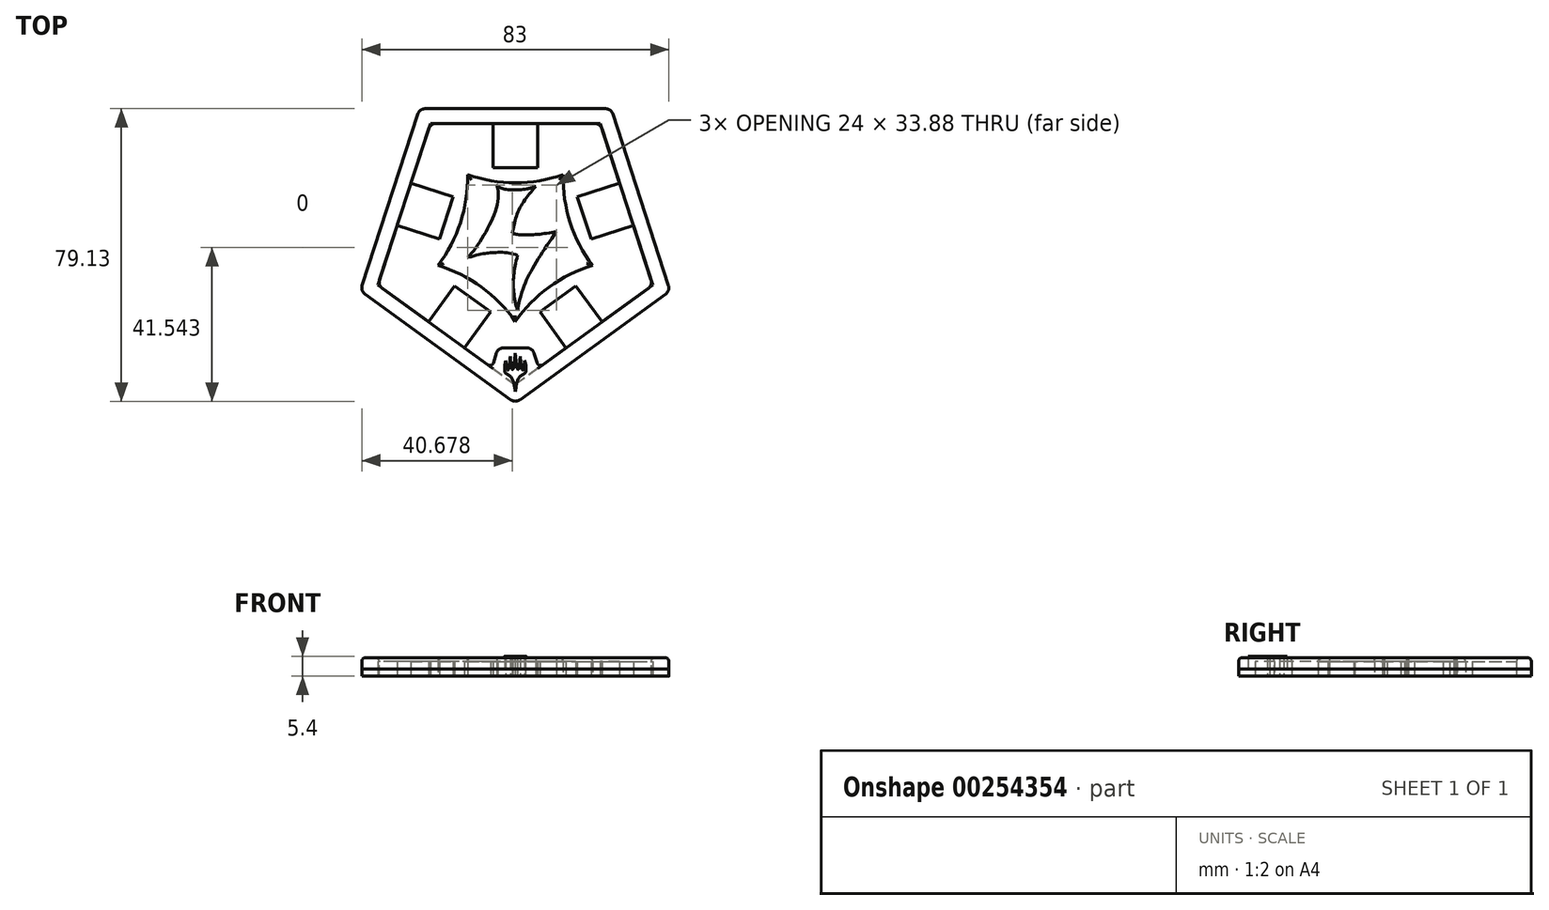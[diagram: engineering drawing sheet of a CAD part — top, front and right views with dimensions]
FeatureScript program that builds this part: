
annotation { "Feature Type Name" : "Feature", "Feature Type Description" : "" }
export const myFeature = defineFeature(function(context is Context, id is Id, definition is map)
    precondition{}
    {
        {
            var Q0;
            Q0=qCreatedBy(makeId("Top.planeOp"),FACE);
            var sketch = newSketch(context, id + "F0", { "sketchPlane" : qUnion([Q0])});
            skCircle(sketch, "E0.cCircle", {"center": v(0, 0) * mm, "radius": 44 * mm, "construction": true});
            skLineSegment(sketch, "E0.0", {"start": v(41.85, -13.6) * mm, "end": v(0, -44) * mm});
            skLineSegment(sketch, "E0.1", {"start": v(0, -44) * mm, "end": v(-41.85, -13.6) * mm});
            skLineSegment(sketch, "E0.2", {"start": v(-41.85, -13.6) * mm, "end": v(-25.86, 35.6) * mm});
            skLineSegment(sketch, "E0.3", {"start": v(-25.86, 35.6) * mm, "end": v(25.86, 35.6) * mm});
            skLineSegment(sketch, "E0.4", {"start": v(25.86, 35.6) * mm, "end": v(41.85, -13.6) * mm});
            skLineSegment(sketch, "E1", {"start": v(-33.85, 11) * mm, "end": v(-24.34, 7.9) * mm, "construction": true});
            skLineSegment(sketch, "E2.bottom", {"start": v(-20.5, 0.35) * mm, "end": v(-31.9, 4.06) * mm});
            skLineSegment(sketch, "E2.top", {"start": v(-16.78, 11.76) * mm, "end": v(-28.2, 15.47) * mm});
            skLineSegment(sketch, "E2.left", {"start": v(-20.5, 0.35) * mm, "end": v(-16.78, 11.76) * mm});
            skLineSegment(sketch, "E2.right", {"start": v(-31.9, 4.06) * mm, "end": v(-28.2, 15.47) * mm});
            skPoint(sketch, "E2.middle", {"position": v(-24.34, 7.9) * mm});
            skLineSegment(sketch, "E3.1.0", {"start": v(-6.66, -19.38) * mm, "end": v(-13.72, -29.09) * mm});
            skLineSegment(sketch, "E3.1.1", {"start": v(-6.66, -19.38) * mm, "end": v(-16.37, -12.33) * mm});
            skLineSegment(sketch, "E3.1.2", {"start": v(-16.37, -12.33) * mm, "end": v(-23.43, -22.04) * mm});
            skLineSegment(sketch, "E3.1.3", {"start": v(-13.72, -29.09) * mm, "end": v(-23.43, -22.04) * mm});
            skPoint(sketch, "E3.1.4", {"position": v(-15.05, -20.7) * mm});
            skLineSegment(sketch, "E3.1.5", {"start": v(-20.92, -28.8) * mm, "end": v(-15.05, -20.7) * mm, "construction": true});
            skLineSegment(sketch, "E3.2.0", {"start": v(16.37, -12.33) * mm, "end": v(23.43, -22.04) * mm});
            skLineSegment(sketch, "E3.2.1", {"start": v(16.37, -12.33) * mm, "end": v(6.66, -19.38) * mm});
            skLineSegment(sketch, "E3.2.2", {"start": v(6.66, -19.38) * mm, "end": v(13.72, -29.09) * mm});
            skLineSegment(sketch, "E3.2.3", {"start": v(23.43, -22.04) * mm, "end": v(13.72, -29.09) * mm});
            skPoint(sketch, "E3.2.4", {"position": v(15.05, -20.7) * mm});
            skLineSegment(sketch, "E3.2.5", {"start": v(20.92, -28.8) * mm, "end": v(15.05, -20.7) * mm, "construction": true});
            skLineSegment(sketch, "E3.3.0", {"start": v(16.78, 11.76) * mm, "end": v(28.2, 15.47) * mm});
            skLineSegment(sketch, "E3.3.1", {"start": v(16.78, 11.76) * mm, "end": v(20.5, 0.35) * mm});
            skLineSegment(sketch, "E3.3.2", {"start": v(20.5, 0.35) * mm, "end": v(31.9, 4.06) * mm});
            skLineSegment(sketch, "E3.3.3", {"start": v(28.2, 15.47) * mm, "end": v(31.9, 4.06) * mm});
            skPoint(sketch, "E3.3.4", {"position": v(24.34, 7.9) * mm});
            skLineSegment(sketch, "E3.3.5", {"start": v(33.85, 11) * mm, "end": v(24.34, 7.9) * mm, "construction": true});
            skLineSegment(sketch, "E3.4.0", {"start": v(-6, 19.6) * mm, "end": v(-6, 31.6) * mm});
            skLineSegment(sketch, "E3.4.1", {"start": v(-6, 19.6) * mm, "end": v(6, 19.6) * mm});
            skLineSegment(sketch, "E3.4.2", {"start": v(6, 19.6) * mm, "end": v(6, 31.6) * mm});
            skLineSegment(sketch, "E3.4.3", {"start": v(-6, 31.6) * mm, "end": v(6, 31.6) * mm});
            skPoint(sketch, "E3.4.4", {"position": v(0, 25.6) * mm});
            skLineSegment(sketch, "E3.4.5", {"start": v(0, 35.6) * mm, "end": v(0, 25.6) * mm, "construction": true});
            skCircle(sketch, "E4.cCircle", {"center": v(0, 0) * mm, "radius": 22 * mm, "construction": true});
            skLineSegment(sketch, "E4.0", {"start": v(20.92, -6.8) * mm, "end": v(0, -22) * mm, "construction": true});
            skLineSegment(sketch, "E4.1", {"start": v(0, -22) * mm, "end": v(-20.92, -6.8) * mm, "construction": true});
            skLineSegment(sketch, "E4.2", {"start": v(-20.92, -6.8) * mm, "end": v(-12.93, 17.8) * mm, "construction": true});
            skLineSegment(sketch, "E4.3", {"start": v(-12.93, 17.8) * mm, "end": v(12.93, 17.8) * mm, "construction": true});
            skLineSegment(sketch, "E4.4", {"start": v(12.93, 17.8) * mm, "end": v(20.92, -6.8) * mm, "construction": true});
            skLineSegment(sketch, "E5", {"start": v(-24.34, 7.9) * mm, "end": v(-14.83, 4.82) * mm, "construction": true});
            skArc(sketch, "E6", {"start": v(-20.92, -6.8) * mm, "mid": v(-14.83, 4.82) * mm, "end": v(-12.93, 17.8) * mm});
            skArc(sketch, "E7.1.0", {"start": v(0, -22) * mm, "mid": v(-9.17, -12.62) * mm, "end": v(-20.92, -6.8) * mm});
            skArc(sketch, "E7.2.0", {"start": v(20.92, -6.8) * mm, "mid": v(9.17, -12.62) * mm, "end": v(0, -22) * mm});
            skArc(sketch, "E7.3.0", {"start": v(12.93, 17.8) * mm, "mid": v(14.83, 4.82) * mm, "end": v(20.92, -6.8) * mm});
            skArc(sketch, "E7.4.0", {"start": v(-12.93, 17.8) * mm, "mid": v(0, 15.6) * mm, "end": v(12.93, 17.8) * mm});
            skLineSegment(sketch, "E8", {"start": v(-41.85, -13.6) * mm, "end": v(0, 0) * mm, "construction": true});
            skLineSegment(sketch, "E9", {"start": v(-31.9, 4.06) * mm, "end": v(-37.14, -12.07) * mm});
            skLineSegment(sketch, "E10", {"start": v(0, 0) * mm, "end": v(-25.86, 35.6) * mm, "construction": true});
            skLineSegment(sketch, "E11", {"start": v(-28.2, 15.47) * mm, "end": v(-22.96, 31.6) * mm});
            skLineSegment(sketch, "E12.1.0", {"start": v(-13.72, -29.09) * mm, "end": v(0, -39.06) * mm});
            skLineSegment(sketch, "E12.1.1", {"start": v(-23.43, -22.04) * mm, "end": v(-37.14, -12.07) * mm});
            skLineSegment(sketch, "E12.2.0", {"start": v(23.43, -22.04) * mm, "end": v(37.14, -12.07) * mm});
            skLineSegment(sketch, "E12.2.1", {"start": v(13.72, -29.09) * mm, "end": v(0, -39.06) * mm});
            skLineSegment(sketch, "E12.3.0", {"start": v(28.2, 15.47) * mm, "end": v(22.96, 31.6) * mm});
            skLineSegment(sketch, "E12.3.1", {"start": v(31.9, 4.06) * mm, "end": v(37.14, -12.07) * mm});
            skLineSegment(sketch, "E12.4.0", {"start": v(-6, 31.6) * mm, "end": v(-22.96, 31.6) * mm});
            skLineSegment(sketch, "E12.4.1", {"start": v(6, 31.6) * mm, "end": v(22.96, 31.6) * mm});
            skSolve(sketch);
        }
        {
            var Q0;
            Q0=qCreatedBy(makeId("Top.planeOp"),FACE);
            var sketch = newSketch(context, id + "F1", { "sketchPlane" : qUnion([Q0])});
            skFitSpline(sketch, "E13", {"points": [v(-5, 14.95) * mm, v(-1.02, 13.68) * mm, v(5.52, 14.64) * mm], "startDerivative": vector(6.48, -7.02) * mm, "endDerivative": vector(9.45, 4.73) * mm});
            skFitSpline(sketch, "E14", {"points": [v(5.52, 14.64) * mm, v(0.97, 8.26) * mm, v(-0.78, 1.88) * mm], "startDerivative": vector(-10.05, -11.93) * mm, "endDerivative": vector(-2.28, -13.44) * mm});
            skFitSpline(sketch, "E15", {"points": [v(-0.78, 1.88) * mm, v(2.89, 1.48) * mm, v(11.18, 2.36) * mm], "startDerivative": vector(7.53, -2.38) * mm, "endDerivative": vector(15.6, 3.22) * mm});
            skFitSpline(sketch, "E16", {"points": [v(11.18, 2.36) * mm, v(4.32, -8.24) * mm, v(0.57, -18.93) * mm], "startDerivative": vector(-15.33, -20.77) * mm, "endDerivative": vector(-6.9, -33.93) * mm});
            skFitSpline(sketch, "E17", {"points": [v(0.57, -18.93) * mm, v(-0.54, -11.83) * mm, v(0.57, -4.1) * mm], "startDerivative": vector(-3.94, 12.93) * mm, "endDerivative": vector(3.74, 16.63) * mm});
            skFitSpline(sketch, "E18", {"points": [v(0.57, -4.1) * mm, v(-5.89, -3.3) * mm, v(-12.82, -4.66) * mm], "startDerivative": vector(-11.71, 5.86) * mm, "endDerivative": vector(-20.63, -6.1) * mm});
            skFitSpline(sketch, "E19", {"points": [v(-12.82, -4.66) * mm, v(-6.6, 4.9) * mm, v(-5, 14.95) * mm], "startDerivative": vector(11.21, 11.67) * mm, "endDerivative": vector(-5.9, 20.2) * mm});
            skSolve(sketch);
        }
        {
            var Q0;
            Q0=qCreatedBy(makeId("Top.planeOp"),FACE);
            var sketch = newSketch(context, id + "F2", { "sketchPlane" : qUnion([Q0])});
            skPoint(sketch, "E20.0", {"position": v(0, 0) * mm});
            skLineSegment(sketch, "E21.0.0", {"start": v(41.85, -13.6) * mm, "end": v(25.86, 35.6) * mm});
            skLineSegment(sketch, "E21.0.1", {"start": v(25.86, 35.6) * mm, "end": v(-25.86, 35.6) * mm});
            skLineSegment(sketch, "E21.0.2", {"start": v(-25.86, 35.6) * mm, "end": v(-41.85, -13.6) * mm});
            skLineSegment(sketch, "E21.0.3", {"start": v(-41.85, -13.6) * mm, "end": v(0, -44) * mm});
            skLineSegment(sketch, "E21.0.4", {"start": v(0, -44) * mm, "end": v(41.85, -13.6) * mm});
            skLineSegment(sketch, "E22.1", {"start": v(-13.72, -29.09) * mm, "end": v(-23.43, -22.04) * mm});
            skLineSegment(sketch, "E22.2", {"start": v(-23.43, -22.04) * mm, "end": v(-37.14, -12.07) * mm});
            skLineSegment(sketch, "E22.3", {"start": v(-31.9, 4.06) * mm, "end": v(-37.14, -12.07) * mm});
            skLineSegment(sketch, "E22.4", {"start": v(-31.9, 4.06) * mm, "end": v(-28.2, 15.47) * mm});
            skLineSegment(sketch, "E22.5", {"start": v(-28.2, 15.47) * mm, "end": v(-22.96, 31.6) * mm});
            skLineSegment(sketch, "E22.7", {"start": v(23.43, -22.04) * mm, "end": v(13.72, -29.09) * mm});
            skLineSegment(sketch, "E22.8", {"start": v(23.43, -22.04) * mm, "end": v(37.14, -12.07) * mm});
            skLineSegment(sketch, "E22.9", {"start": v(31.9, 4.06) * mm, "end": v(37.14, -12.07) * mm});
            skLineSegment(sketch, "E22.10", {"start": v(28.2, 15.47) * mm, "end": v(31.9, 4.06) * mm});
            skLineSegment(sketch, "E22.11", {"start": v(28.2, 15.47) * mm, "end": v(22.96, 31.6) * mm});
            skLineSegment(sketch, "E22.12", {"start": v(6, 31.6) * mm, "end": v(22.96, 31.6) * mm});
            skLineSegment(sketch, "E22.13", {"start": v(-6, 31.6) * mm, "end": v(6, 31.6) * mm});
            skLineSegment(sketch, "E22.14", {"start": v(-6, 31.6) * mm, "end": v(-22.96, 31.6) * mm});
            skLineSegment(sketch, "E23", {"start": v(-13.72, -29.09) * mm, "end": v(-6.31, -34.47) * mm});
            skLineSegment(sketch, "E24", {"start": v(-6.31, -34.47) * mm, "end": v(-4.65, -29.09) * mm});
            skLineSegment(sketch, "E25", {"start": v(13.72, -29.09) * mm, "end": v(6.31, -34.47) * mm});
            skLineSegment(sketch, "E26", {"start": v(6.31, -34.47) * mm, "end": v(4.57, -29.09) * mm});
            skLineSegment(sketch, "E27", {"start": v(4.57, -29.09) * mm, "end": v(-4.65, -29.09) * mm});
            skSolve(sketch);
        }
        {
            var Q0;
            Q0=qCreatedBy(makeId("Top.planeOp"),FACE);
            var sketch = newSketch(context, id + "F3", { "sketchPlane" : qUnion([Q0])});
            skFitSpline(sketch, "E28", {"points": [v(0, -30.45) * mm, v(-0.66, -34.88) * mm, v(-1.34, -31.36) * mm], "startDerivative": vector(-1.52, -19.16) * mm, "endDerivative": vector(-1.65, 22.93) * mm});
            skFitSpline(sketch, "E29", {"points": [v(-1.34, -31.36) * mm, v(-2.03, -35.13) * mm, v(-2.53, -32.49) * mm], "startDerivative": vector(-1.22, -16.23) * mm, "endDerivative": vector(-0.98, 14.27) * mm});
            skFitSpline(sketch, "E30", {"points": [v(-2.53, -32.49) * mm, v(-2.9, -34.67) * mm, v(-2.8, -35.7) * mm], "startDerivative": vector(-1.89, -5.29) * mm, "endDerivative": vector(0.95, -1.62) * mm});
            skFitSpline(sketch, "E31", {"points": [v(-2.8, -35.7) * mm, v(-1.08, -37.06) * mm, v(0, -40.97) * mm], "startDerivative": vector(2.36, -2.75) * mm, "endDerivative": vector(1.27, -7.94) * mm});
            skFitSpline(sketch, "E32.MirrorCS", {"points": [v(0, -30.45) * mm, v(0.66, -34.88) * mm, v(1.34, -31.36) * mm], "startDerivative": vector(1.52, -19.16) * mm, "endDerivative": vector(1.65, 22.93) * mm});
            skFitSpline(sketch, "E33.MirrorCS", {"points": [v(1.34, -31.36) * mm, v(2.03, -35.13) * mm, v(2.53, -32.49) * mm], "startDerivative": vector(1.22, -16.23) * mm, "endDerivative": vector(0.98, 14.27) * mm});
            skFitSpline(sketch, "E34.MirrorCS", {"points": [v(2.53, -32.49) * mm, v(2.9, -34.67) * mm, v(2.8, -35.7) * mm], "startDerivative": vector(1.89, -5.29) * mm, "endDerivative": vector(-0.95, -1.62) * mm});
            skFitSpline(sketch, "E35.MirrorCS", {"points": [v(2.8, -35.7) * mm, v(1.08, -37.06) * mm, v(0, -40.97) * mm], "startDerivative": vector(-2.36, -2.75) * mm, "endDerivative": vector(-1.27, -7.94) * mm});
            skSolve(sketch);
        }
        {
            var Q0;
            Q0=makeQuery(id+"F2.imprint","IMPRINT",FACE,{"disambiguationData":[TD([[makeQuery(id+"F2.imprint","IMPRINT",EDGE,{"derivedFrom":sQuery(id+"F2.wireOp",EDGE,"E21.0.0")}),1.0]])]});
            var Q1;
            Q1=makeQuery(id+"F0.imprint","IMPRINT",FACE,{"disambiguationData":[TD([[makeQuery(id+"F0.imprint","IMPRINT",EDGE,{"derivedFrom":sQuery(id+"F0.wireOp",EDGE,"E6")}),-1.0]])]});
            var Q2;
            Q2=makeQuery(id+"F0.imprint","IMPRINT",FACE,{"disambiguationData":[TD([[makeQuery(id+"F0.imprint","IMPRINT",EDGE,{"derivedFrom":sQuery(id+"F0.wireOp",EDGE,"E2.bottom")}),1.0]])]});
            var Q3;
            Q3=makeQuery(id+"F2.imprint","IMPRINT",FACE,{"disambiguationData":[TD([[makeQuery(id+"F2.imprint","IMPRINT",EDGE,{"derivedFrom":sQuery(id+"F2.wireOp",EDGE,"E22.1")}),-1.0]])]});
            extrude(context, id + "F4", {"entities" : qUnion([Q0, Q1, Q2, Q3]), "depth" : 2 * mm});
        }
        {
            var Q0;
            Q0 = qSketchRegion(id + "F2", true);
            extrude(context, id + "F5", {"entities" : qUnion([Q0]), "depth" : 5 * mm});
        }
        {
            var Q0;
            Q0=makeQuery(id+"F4.opExtrude","CAP_FACE",FACE,{"disambiguationData":[OSD([sQuery(id+"F0.wireOp",EDGE,"E2.bottom"),sQuery(id+"F0.wireOp",EDGE,"E2.top"),sQuery(id+"F0.wireOp",EDGE,"E2.left"),sQuery(id+"F0.wireOp",EDGE,"E3.1.0"),sQuery(id+"F0.wireOp",EDGE,"E3.1.1"),sQuery(id+"F0.wireOp",EDGE,"E3.1.2"),sQuery(id+"F0.wireOp",EDGE,"E3.2.0"),sQuery(id+"F0.wireOp",EDGE,"E3.2.1"),sQuery(id+"F0.wireOp",EDGE,"E3.2.2"),sQuery(id+"F0.wireOp",EDGE,"E3.3.0"),sQuery(id+"F0.wireOp",EDGE,"E3.3.1"),sQuery(id+"F0.wireOp",EDGE,"E3.3.2"),sQuery(id+"F0.wireOp",EDGE,"E3.4.0"),sQuery(id+"F0.wireOp",EDGE,"E3.4.1"),sQuery(id+"F0.wireOp",EDGE,"E3.4.2"),sQuery(id+"F0.wireOp",EDGE,"E9"),sQuery(id+"F0.wireOp",EDGE,"E11"),sQuery(id+"F0.wireOp",EDGE,"E12.1.0"),sQuery(id+"F0.wireOp",EDGE,"E12.1.1"),sQuery(id+"F0.wireOp",EDGE,"E12.2.0"),sQuery(id+"F0.wireOp",EDGE,"E12.2.1"),sQuery(id+"F0.wireOp",EDGE,"E12.3.0"),sQuery(id+"F0.wireOp",EDGE,"E12.3.1"),sQuery(id+"F0.wireOp",EDGE,"E12.4.0"),sQuery(id+"F0.wireOp",EDGE,"E12.4.1")])],"isStart":false});
            extrude(context, id + "F6", {"entities" : qUnion([Q0]), "depth" : 2 * mm});
        }
        {
            var Q0;
            Q0=qCreatedBy(makeId("Top.planeOp"),FACE);
            var sketch = newSketch(context, id + "F7", { "sketchPlane" : qUnion([Q0])});
            skArc(sketch, "E36.0", {"start": v(-20.92, -6.8) * mm, "mid": v(-14.83, 4.82) * mm, "end": v(-12.93, 17.8) * mm});
            skArc(sketch, "E36.1", {"start": v(0, -22) * mm, "mid": v(-9.17, -12.62) * mm, "end": v(-20.92, -6.8) * mm});
            skArc(sketch, "E36.2", {"start": v(20.92, -6.8) * mm, "mid": v(9.17, -12.62) * mm, "end": v(0, -22) * mm});
            skArc(sketch, "E36.3", {"start": v(12.93, 17.8) * mm, "mid": v(14.83, 4.82) * mm, "end": v(20.92, -6.8) * mm});
            skArc(sketch, "E36.4", {"start": v(-12.93, 17.8) * mm, "mid": v(0, 15.6) * mm, "end": v(12.93, 17.8) * mm});
            skSolve(sketch);
        }
        {
            var Q0;
            Q0 = qSketchRegion(id + "F7", true);
            extrude(context, id + "F8", {"entities" : qUnion([Q0]), "depth" : 5 * mm});
        }
        {
            var Q0;
            Q0 = qSketchRegion(id + "F1", true);
            extrude(context, id + "F9", {"entities" : qUnion([Q0]), "operationType" : NewBodyOperationType.REMOVE, "endBound" : BoundingType.THROUGH_ALL, "depth" : 25 * mm});
        }
        {
            var Q0;
            Q0 = qSketchRegion(id + "F3", true);
            var Q1;
            Q1=makeQuery(id+"F5.opExtrude","CAP_FACE",FACE,{"disambiguationData":[OSD([sQuery(id+"F2.wireOp",EDGE,"E21.0.0"),sQuery(id+"F2.wireOp",EDGE,"E21.0.1"),sQuery(id+"F2.wireOp",EDGE,"E21.0.2"),sQuery(id+"F2.wireOp",EDGE,"E21.0.3"),sQuery(id+"F2.wireOp",EDGE,"E21.0.4"),sQuery(id+"F2.wireOp",EDGE,"E22.1"),sQuery(id+"F2.wireOp",EDGE,"E22.2"),sQuery(id+"F2.wireOp",EDGE,"E22.3"),sQuery(id+"F2.wireOp",EDGE,"E22.4"),sQuery(id+"F2.wireOp",EDGE,"E22.5"),sQuery(id+"F2.wireOp",EDGE,"E22.7"),sQuery(id+"F2.wireOp",EDGE,"E22.8"),sQuery(id+"F2.wireOp",EDGE,"E22.9"),sQuery(id+"F2.wireOp",EDGE,"E22.10"),sQuery(id+"F2.wireOp",EDGE,"E22.11"),sQuery(id+"F2.wireOp",EDGE,"E22.12"),sQuery(id+"F2.wireOp",EDGE,"E22.13"),sQuery(id+"F2.wireOp",EDGE,"E22.14"),sQuery(id+"F2.wireOp",EDGE,"E23"),sQuery(id+"F2.wireOp",EDGE,"E24"),sQuery(id+"F2.wireOp",EDGE,"E25"),sQuery(id+"F2.wireOp",EDGE,"E26"),sQuery(id+"F2.wireOp",EDGE,"E27")])],"isStart":false});
            extrude(context, id + "F10", {"entities" : qUnion([Q0]), "endBoundEntityFace" : qUnion([Q1]), "depth" : 5.4 * mm});
        }
        {
            var Q0;
            Q0=makeQuery(id+"F8.opExtrude","CAP_EDGE",EDGE,{"disambiguationData":[OSD([sQuery(id+"F7.wireOp",EDGE,"E36.1")])],"isStart":false});
            var Q1;
            Q1=makeQuery(id+"F8.opExtrude","CAP_EDGE",EDGE,{"disambiguationData":[OSD([sQuery(id+"F7.wireOp",EDGE,"E36.2")])],"isStart":false});
            var Q2;
            Q2=makeQuery(id+"F8.opExtrude","CAP_EDGE",EDGE,{"disambiguationData":[OSD([sQuery(id+"F7.wireOp",EDGE,"E36.3")])],"isStart":false});
            var Q3;
            Q3=makeQuery(id+"F8.opExtrude","CAP_EDGE",EDGE,{"disambiguationData":[OSD([sQuery(id+"F7.wireOp",EDGE,"E36.4")])],"isStart":false});
            var Q4;
            Q4=makeQuery(id+"F8.opExtrude","CAP_EDGE",EDGE,{"disambiguationData":[OSD([sQuery(id+"F7.wireOp",EDGE,"E36.0")])],"isStart":false});
            fillet(context, id + "F11", {"entities" : qUnion([Q0, Q1, Q2, Q3, Q4]), "radius" : 1 * mm, "tangentPropagation" : true, "allowEdgeOverflow" : false});
        }
        {
            var Q0;
            Q0=makeQuery(id+"F5.opExtrude","SWEPT_EDGE",EDGE,{"disambiguationData":[OSD([sQuery(id+"F2.wireOp",EDGE,"E21.0.2"),sQuery(id+"F2.wireOp",EDGE,"E21.0.3")])]});
            var Q1;
            Q1=makeQuery(id+"F4.opExtrude","SWEPT_EDGE",EDGE,{"disambiguationData":[OSD([sQuery(id+"F2.wireOp",EDGE,"E21.0.2"),sQuery(id+"F2.wireOp",EDGE,"E21.0.3")])]});
            var Q2;
            Q2=makeQuery(id+"F4.opExtrude","SWEPT_EDGE",EDGE,{"disambiguationData":[OSD([sQuery(id+"F2.wireOp",EDGE,"E21.0.3"),sQuery(id+"F2.wireOp",EDGE,"E21.0.4")])]});
            var Q3;
            Q3=makeQuery(id+"F5.opExtrude","SWEPT_EDGE",EDGE,{"disambiguationData":[OSD([sQuery(id+"F2.wireOp",EDGE,"E21.0.3"),sQuery(id+"F2.wireOp",EDGE,"E21.0.4")])]});
            var Q4;
            Q4=makeQuery(id+"F5.opExtrude","SWEPT_EDGE",EDGE,{"disambiguationData":[OSD([sQuery(id+"F2.wireOp",EDGE,"E21.0.0"),sQuery(id+"F2.wireOp",EDGE,"E21.0.4")])]});
            var Q5;
            Q5=makeQuery(id+"F4.opExtrude","SWEPT_EDGE",EDGE,{"disambiguationData":[OSD([sQuery(id+"F2.wireOp",EDGE,"E21.0.0"),sQuery(id+"F2.wireOp",EDGE,"E21.0.4")])]});
            var Q6;
            Q6=makeQuery(id+"F5.opExtrude","SWEPT_EDGE",EDGE,{"disambiguationData":[OSD([sQuery(id+"F2.wireOp",EDGE,"E21.0.1"),sQuery(id+"F2.wireOp",EDGE,"E21.0.2")])]});
            var Q7;
            Q7=makeQuery(id+"F4.opExtrude","SWEPT_EDGE",EDGE,{"disambiguationData":[OSD([sQuery(id+"F2.wireOp",EDGE,"E21.0.1"),sQuery(id+"F2.wireOp",EDGE,"E21.0.2")])]});
            var Q8;
            Q8=makeQuery(id+"F5.opExtrude","SWEPT_EDGE",EDGE,{"disambiguationData":[OSD([sQuery(id+"F2.wireOp",EDGE,"E21.0.0"),sQuery(id+"F2.wireOp",EDGE,"E21.0.1")])]});
            var Q9;
            Q9=makeQuery(id+"F4.opExtrude","SWEPT_EDGE",EDGE,{"disambiguationData":[OSD([sQuery(id+"F2.wireOp",EDGE,"E21.0.0"),sQuery(id+"F2.wireOp",EDGE,"E21.0.1")])]});
            var Q10;
            Q10=makeQuery(id+"F5.opExtrude","SWEPT_EDGE",EDGE,{"disambiguationData":[OSD([sQuery(id+"F2.wireOp",EDGE,"E22.11"),sQuery(id+"F2.wireOp",EDGE,"E22.12")])]});
            var Q11;
            Q11=makeQuery(id+"F5.opExtrude","SWEPT_EDGE",EDGE,{"disambiguationData":[OSD([sQuery(id+"F2.wireOp",EDGE,"E22.5"),sQuery(id+"F2.wireOp",EDGE,"E22.14")])]});
            var Q12;
            Q12=makeQuery(id+"F5.opExtrude","SWEPT_EDGE",EDGE,{"disambiguationData":[OSD([sQuery(id+"F2.wireOp",EDGE,"E22.2"),sQuery(id+"F2.wireOp",EDGE,"E22.3")])]});
            var Q13;
            Q13=makeQuery(id+"F5.opExtrude","SWEPT_EDGE",EDGE,{"disambiguationData":[OSD([sQuery(id+"F2.wireOp",EDGE,"E22.8"),sQuery(id+"F2.wireOp",EDGE,"E22.9")])]});
            fillet(context, id + "F12", {"entities" : qUnion([Q0, Q1, Q2, Q3, Q4, Q5, Q6, Q7, Q8, Q9, Q10, Q11, Q12, Q13]), "radius" : 2 * mm, "tangentPropagation" : true, "allowEdgeOverflow" : false});
        }
        {
            var Q0;
            Q0=makeQuery(id+"F5.opExtrude","SWEPT_EDGE",EDGE,{"disambiguationData":[OSD([sQuery(id+"F2.wireOp",EDGE,"E24"),sQuery(id+"F2.wireOp",EDGE,"E27")])]});
            var Q1;
            Q1=makeQuery(id+"F5.opExtrude","SWEPT_EDGE",EDGE,{"disambiguationData":[OSD([sQuery(id+"F2.wireOp",EDGE,"E26"),sQuery(id+"F2.wireOp",EDGE,"E27")])]});
            fillet(context, id + "F13", {"entities" : qUnion([Q0, Q1]), "radius" : 2 * mm, "tangentPropagation" : true, "allowEdgeOverflow" : false});
        }
        {
            var Q0;
            Q0=makeQuery(id+"F5.opExtrude","SWEPT_EDGE",EDGE,{"disambiguationData":[OSD([sQuery(id+"F2.wireOp",EDGE,"E23"),sQuery(id+"F2.wireOp",EDGE,"E24")])]});
            var Q1;
            Q1=makeQuery(id+"F5.opExtrude","SWEPT_EDGE",EDGE,{"disambiguationData":[OSD([sQuery(id+"F2.wireOp",EDGE,"E25"),sQuery(id+"F2.wireOp",EDGE,"E26")])]});
            fillet(context, id + "F14", {"entities" : qUnion([Q0, Q1]), "radius" : 1 * mm, "tangentPropagation" : true, "allowEdgeOverflow" : false});
        }
        {
            var Q0;
            {var subQ0=sQuery(id+"F2.wireOp",EDGE,"E21.0.2");var subQ1=sQuery(id+"F2.wireOp",EDGE,"E21.0.1");Q0=makeQuery(id+"F12.opFillet","BLEND_EDGE",EDGE,{"blendedFrom":[makeQuery(id+"F5.opExtrude","SWEPT_EDGE",EDGE,{"disambiguationData":[OSD([subQ1,subQ0])]}),makeQuery(id+"F5.opExtrude","CAP_FACE",FACE,{"disambiguationData":[OSD([sQuery(id+"F2.wireOp",EDGE,"E21.0.0"),subQ1,subQ0,sQuery(id+"F2.wireOp",EDGE,"E21.0.3"),sQuery(id+"F2.wireOp",EDGE,"E21.0.4"),sQuery(id+"F2.wireOp",EDGE,"E22.1"),sQuery(id+"F2.wireOp",EDGE,"E22.2"),sQuery(id+"F2.wireOp",EDGE,"E22.3"),sQuery(id+"F2.wireOp",EDGE,"E22.4"),sQuery(id+"F2.wireOp",EDGE,"E22.5"),sQuery(id+"F2.wireOp",EDGE,"E22.7"),sQuery(id+"F2.wireOp",EDGE,"E22.8"),sQuery(id+"F2.wireOp",EDGE,"E22.9"),sQuery(id+"F2.wireOp",EDGE,"E22.10"),sQuery(id+"F2.wireOp",EDGE,"E22.11"),sQuery(id+"F2.wireOp",EDGE,"E22.12"),sQuery(id+"F2.wireOp",EDGE,"E22.13"),sQuery(id+"F2.wireOp",EDGE,"E22.14"),sQuery(id+"F2.wireOp",EDGE,"E23"),sQuery(id+"F2.wireOp",EDGE,"E24"),sQuery(id+"F2.wireOp",EDGE,"E25"),sQuery(id+"F2.wireOp",EDGE,"E26"),sQuery(id+"F2.wireOp",EDGE,"E27")])],"isStart":false})],"blendedInto":[makeQuery(id+"F5.opExtrude","CAP_FACE",FACE,{"disambiguationData":[OSD([sQuery(id+"F2.wireOp",EDGE,"E21.0.0"),subQ1,subQ0,sQuery(id+"F2.wireOp",EDGE,"E21.0.3"),sQuery(id+"F2.wireOp",EDGE,"E21.0.4"),sQuery(id+"F2.wireOp",EDGE,"E22.1"),sQuery(id+"F2.wireOp",EDGE,"E22.2"),sQuery(id+"F2.wireOp",EDGE,"E22.3"),sQuery(id+"F2.wireOp",EDGE,"E22.4"),sQuery(id+"F2.wireOp",EDGE,"E22.5"),sQuery(id+"F2.wireOp",EDGE,"E22.7"),sQuery(id+"F2.wireOp",EDGE,"E22.8"),sQuery(id+"F2.wireOp",EDGE,"E22.9"),sQuery(id+"F2.wireOp",EDGE,"E22.10"),sQuery(id+"F2.wireOp",EDGE,"E22.11"),sQuery(id+"F2.wireOp",EDGE,"E22.12"),sQuery(id+"F2.wireOp",EDGE,"E22.13"),sQuery(id+"F2.wireOp",EDGE,"E22.14"),sQuery(id+"F2.wireOp",EDGE,"E23"),sQuery(id+"F2.wireOp",EDGE,"E24"),sQuery(id+"F2.wireOp",EDGE,"E25"),sQuery(id+"F2.wireOp",EDGE,"E26"),sQuery(id+"F2.wireOp",EDGE,"E27")])],"isStart":false})]});}
            fillet(context, id + "F15", {"entities" : qUnion([Q0]), "radius" : 1 * mm, "tangentPropagation" : true, "allowEdgeOverflow" : false});
        }
        {
            var Q0;
            {var subQ0=sQuery(id+"F2.wireOp",EDGE,"E22.14");var subQ1=sQuery(id+"F2.wireOp",EDGE,"E22.5");Q0=makeQuery(id+"F12.opFillet","BLEND_EDGE",EDGE,{"blendedFrom":[makeQuery(id+"F5.opExtrude","SWEPT_EDGE",EDGE,{"disambiguationData":[OSD([subQ1,subQ0])]}),makeQuery(id+"F5.opExtrude","CAP_FACE",FACE,{"disambiguationData":[OSD([sQuery(id+"F2.wireOp",EDGE,"E21.0.0"),sQuery(id+"F2.wireOp",EDGE,"E21.0.1"),sQuery(id+"F2.wireOp",EDGE,"E21.0.2"),sQuery(id+"F2.wireOp",EDGE,"E21.0.3"),sQuery(id+"F2.wireOp",EDGE,"E21.0.4"),sQuery(id+"F2.wireOp",EDGE,"E22.1"),sQuery(id+"F2.wireOp",EDGE,"E22.2"),sQuery(id+"F2.wireOp",EDGE,"E22.3"),sQuery(id+"F2.wireOp",EDGE,"E22.4"),subQ1,sQuery(id+"F2.wireOp",EDGE,"E22.7"),sQuery(id+"F2.wireOp",EDGE,"E22.8"),sQuery(id+"F2.wireOp",EDGE,"E22.9"),sQuery(id+"F2.wireOp",EDGE,"E22.10"),sQuery(id+"F2.wireOp",EDGE,"E22.11"),sQuery(id+"F2.wireOp",EDGE,"E22.12"),sQuery(id+"F2.wireOp",EDGE,"E22.13"),subQ0,sQuery(id+"F2.wireOp",EDGE,"E23"),sQuery(id+"F2.wireOp",EDGE,"E24"),sQuery(id+"F2.wireOp",EDGE,"E25"),sQuery(id+"F2.wireOp",EDGE,"E26"),sQuery(id+"F2.wireOp",EDGE,"E27")])],"isStart":false})],"blendedInto":[makeQuery(id+"F5.opExtrude","CAP_FACE",FACE,{"disambiguationData":[OSD([sQuery(id+"F2.wireOp",EDGE,"E21.0.0"),sQuery(id+"F2.wireOp",EDGE,"E21.0.1"),sQuery(id+"F2.wireOp",EDGE,"E21.0.2"),sQuery(id+"F2.wireOp",EDGE,"E21.0.3"),sQuery(id+"F2.wireOp",EDGE,"E21.0.4"),sQuery(id+"F2.wireOp",EDGE,"E22.1"),sQuery(id+"F2.wireOp",EDGE,"E22.2"),sQuery(id+"F2.wireOp",EDGE,"E22.3"),sQuery(id+"F2.wireOp",EDGE,"E22.4"),subQ1,sQuery(id+"F2.wireOp",EDGE,"E22.7"),sQuery(id+"F2.wireOp",EDGE,"E22.8"),sQuery(id+"F2.wireOp",EDGE,"E22.9"),sQuery(id+"F2.wireOp",EDGE,"E22.10"),sQuery(id+"F2.wireOp",EDGE,"E22.11"),sQuery(id+"F2.wireOp",EDGE,"E22.12"),sQuery(id+"F2.wireOp",EDGE,"E22.13"),subQ0,sQuery(id+"F2.wireOp",EDGE,"E23"),sQuery(id+"F2.wireOp",EDGE,"E24"),sQuery(id+"F2.wireOp",EDGE,"E25"),sQuery(id+"F2.wireOp",EDGE,"E26"),sQuery(id+"F2.wireOp",EDGE,"E27")])],"isStart":false})]});}
            fillet(context, id + "F16", {"entities" : qUnion([Q0]), "radius" : 1 * mm, "tangentPropagation" : true, "allowEdgeOverflow" : false});
        }
    });
